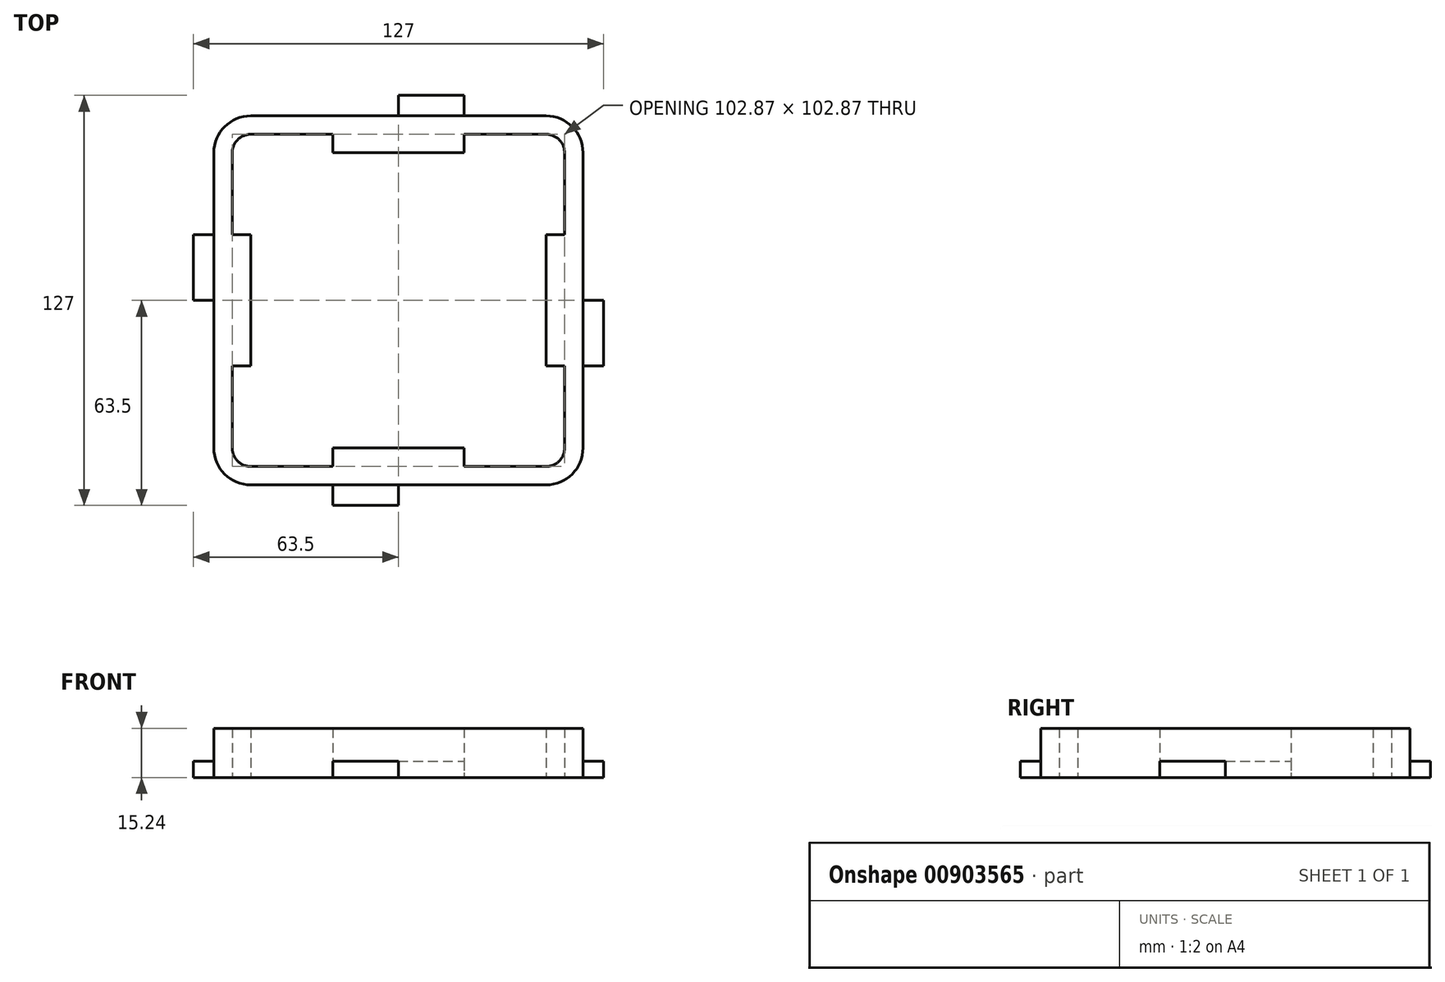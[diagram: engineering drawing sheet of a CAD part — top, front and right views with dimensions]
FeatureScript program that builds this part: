
annotation { "Feature Type Name" : "Feature", "Feature Type Description" : "" }
export const myFeature = defineFeature(function(context is Context, id is Id, definition is map)
    precondition{}
    {
        {
            var Q0;
            Q0=qCreatedBy(makeId("Top.planeOp"),FACE);
            var sketch = newSketch(context, id + "F0", { "sketchPlane" : qUnion([Q0])});
            skLineSegment(sketch, "E0.bottom", {"start": v(-45.72, 45.72) * mm, "end": v(45.72, 45.72) * mm, "construction": true});
            skLineSegment(sketch, "E0.top", {"start": v(-45.72, -45.72) * mm, "end": v(45.72, -45.72) * mm, "construction": true});
            skLineSegment(sketch, "E0.left", {"start": v(-45.72, 45.72) * mm, "end": v(-45.72, -45.72) * mm, "construction": true});
            skLineSegment(sketch, "E0.right", {"start": v(45.72, 45.72) * mm, "end": v(45.72, -45.72) * mm, "construction": true});
            skPoint(sketch, "E0.middle", {"position": v(0, 0) * mm});
            skLineSegment(sketch, "E1.top", {"start": v(57.15, -57.15) * mm, "end": v(-57.15, -57.15) * mm, "construction": true});
            skLineSegment(sketch, "E1.left", {"start": v(57.15, 57.15) * mm, "end": v(57.15, -57.15) * mm, "construction": true});
            skLineSegment(sketch, "E2.bottom", {"start": v(0, 57.15) * mm, "end": v(-20.32, 57.15) * mm});
            skLineSegment(sketch, "E2.top", {"start": v(0, 45.72) * mm, "end": v(-20.32, 45.72) * mm});
            skLineSegment(sketch, "E2.left", {"start": v(0, 57.15) * mm, "end": v(0, 45.72) * mm});
            skLineSegment(sketch, "E2.right", {"start": v(-20.32, 51.44) * mm, "end": v(-20.32, 45.72) * mm});
            skLineSegment(sketch, "E3.bottom", {"start": v(-57.15, 0) * mm, "end": v(-45.72, 0) * mm});
            skLineSegment(sketch, "E3.top", {"start": v(-57.15, 20.32) * mm, "end": v(-45.72, 20.32) * mm});
            skLineSegment(sketch, "E3.left", {"start": v(-57.15, 0) * mm, "end": v(-57.15, 20.32) * mm});
            skLineSegment(sketch, "E3.right", {"start": v(-45.72, 0) * mm, "end": v(-45.72, 20.32) * mm});
            skLineSegment(sketch, "E4", {"start": v(-57.15, 20.32) * mm, "end": v(-57.15, 45.72) * mm});
            skLineSegment(sketch, "E5", {"start": v(-45.72, 57.15) * mm, "end": v(-20.32, 57.15) * mm});
            skLineSegment(sketch, "E6", {"start": v(-20.32, 51.44) * mm, "end": v(-45.72, 51.44) * mm});
            skPoint(sketch, "E6.endSnap0", {"position": v(-20.32, 51.44) * mm});
            skPoint(sketch, "E7.endSnap0", {"position": v(-51.44, 20.32) * mm});
            skLineSegment(sketch, "E8", {"start": v(-51.44, 45.76) * mm, "end": v(-51.44, 20.32) * mm});
            skPoint(sketch, "E9.orphan", {"position": v(-45.72, 51.44) * mm});
            skArc(sketch, "E10", {"start": v(-51.44, 45.76) * mm, "mid": v(-49.76, 49.79) * mm, "end": v(-45.72, 51.44) * mm});
            skArc(sketch, "E11", {"start": v(-57.15, 45.72) * mm, "mid": v(-53.8, 53.8) * mm, "end": v(-45.72, 57.15) * mm});
            skLineSegment(sketch, "E12.bottom", {"start": v(-20.32, 57.15) * mm, "end": v(0, 57.15) * mm});
            skLineSegment(sketch, "E12.top", {"start": v(-20.32, 63.5) * mm, "end": v(0, 63.5) * mm});
            skLineSegment(sketch, "E12.left", {"start": v(-20.32, 57.15) * mm, "end": v(-20.32, 63.5) * mm});
            skLineSegment(sketch, "E12.right", {"start": v(0, 57.15) * mm, "end": v(0, 63.5) * mm});
            skLineSegment(sketch, "E13.bottom", {"start": v(-57.15, 0) * mm, "end": v(-63.5, 0) * mm});
            skLineSegment(sketch, "E13.top", {"start": v(-57.15, 20.32) * mm, "end": v(-63.5, 20.32) * mm});
            skLineSegment(sketch, "E13.right", {"start": v(-63.5, 0) * mm, "end": v(-63.5, 20.32) * mm});
            skSolve(sketch);
        }
        {
            var Q0;
            Q0=makeQuery(id+"F0.imprint","IMPRINT",FACE,{"disambiguationData":[TD([[makeQuery(id+"F0.imprint","IMPRINT",EDGE,{"derivedFrom":sQuery(id+"F0.wireOp",EDGE,"E2.bottom")}),1.0]])]});
            var Q1;
            Q1=makeQuery(id+"F0.imprint","IMPRINT",FACE,{"disambiguationData":[TD([[makeQuery(id+"F0.imprint","IMPRINT",EDGE,{"derivedFrom":sQuery(id+"F0.wireOp",EDGE,"E3.bottom")}),1.0]])]});
            var Q2;
            Q2=makeQuery(id+"F0.imprint","IMPRINT",FACE,{"disambiguationData":[TD([[makeQuery(id+"F0.imprint","IMPRINT",EDGE,{"derivedFrom":sQuery(id+"F0.wireOp",EDGE,"E2.top")}),-1.0]])]});
            extrude(context, id + "F1", {"entities" : qUnion([Q0, Q1, Q2]), "depth" : 15.24 * mm, "offsetDistance" : 25.4 * mm});
        }
        {
            var Q0;
            Q0=makeQuery(id+"F0.imprint","IMPRINT",FACE,{"disambiguationData":[TD([[makeQuery(id+"F0.imprint","IMPRINT",EDGE,{"derivedFrom":sQuery(id+"F0.wireOp",EDGE,"E13.bottom")}),-1.0]])]});
            var Q1;
            Q1=makeQuery(id+"F0.imprint","IMPRINT",FACE,{"disambiguationData":[TD([[makeQuery(id+"F0.imprint","IMPRINT",EDGE,{"derivedFrom":sQuery(id+"F0.wireOp",EDGE,"E12.bottom")}),1.0]])]});
            extrude(context, id + "F2", {"entities" : qUnion([Q0, Q1]), "operationType" : NewBodyOperationType.ADD, "depth" : 5.08 * mm, "offsetDistance" : 25.4 * mm});
        }
        {
            var Q0;
            Q0=qCreatedBy(makeId("Right.planeOp"),FACE);
            var sketch = newSketch(context, id + "F3", { "sketchPlane" : qUnion([Q0])});
            skLineSegment(sketch, "E14", {"start": v(0, 67.6) * mm, "end": v(0, 35.2) * mm, "construction": true});
            skSolve(sketch);
        }
        {
            var Q0;
            Q0=makeQuery(id+"F1.opExtrude","SWEPT_BODY",BODY,{"disambiguationData":[OSD([sQuery(id+"F0.wireOp",EDGE,"E2.top"),sQuery(id+"F0.wireOp",EDGE,"E2.left"),sQuery(id+"F0.wireOp",EDGE,"E2.right"),sQuery(id+"F0.wireOp",EDGE,"E3.bottom"),sQuery(id+"F0.wireOp",EDGE,"E3.top"),sQuery(id+"F0.wireOp",EDGE,"E3.right"),sQuery(id+"F0.wireOp",EDGE,"E4"),sQuery(id+"F0.wireOp",EDGE,"E5"),sQuery(id+"F0.wireOp",EDGE,"E6"),sQuery(id+"F0.wireOp",EDGE,"E8"),sQuery(id+"F0.wireOp",EDGE,"E10"),sQuery(id+"F0.wireOp",EDGE,"E11"),sQuery(id+"F0.wireOp",EDGE,"E12.bottom"),sQuery(id+"F0.wireOp",EDGE,"E3.left")])]});
            var Q1;
            Q1=sQuery(id+"F3.wireOp",EDGE,"E14");
            circularPattern(context, id + "F4", {"operationType" : NewBodyOperationType.ADD, "entities" : qUnion([Q0]), "axis" : qUnion([Q1]), "angle" : 360 * degree, "instanceCount" : 4, "equalSpace" : true});
        }
    });
